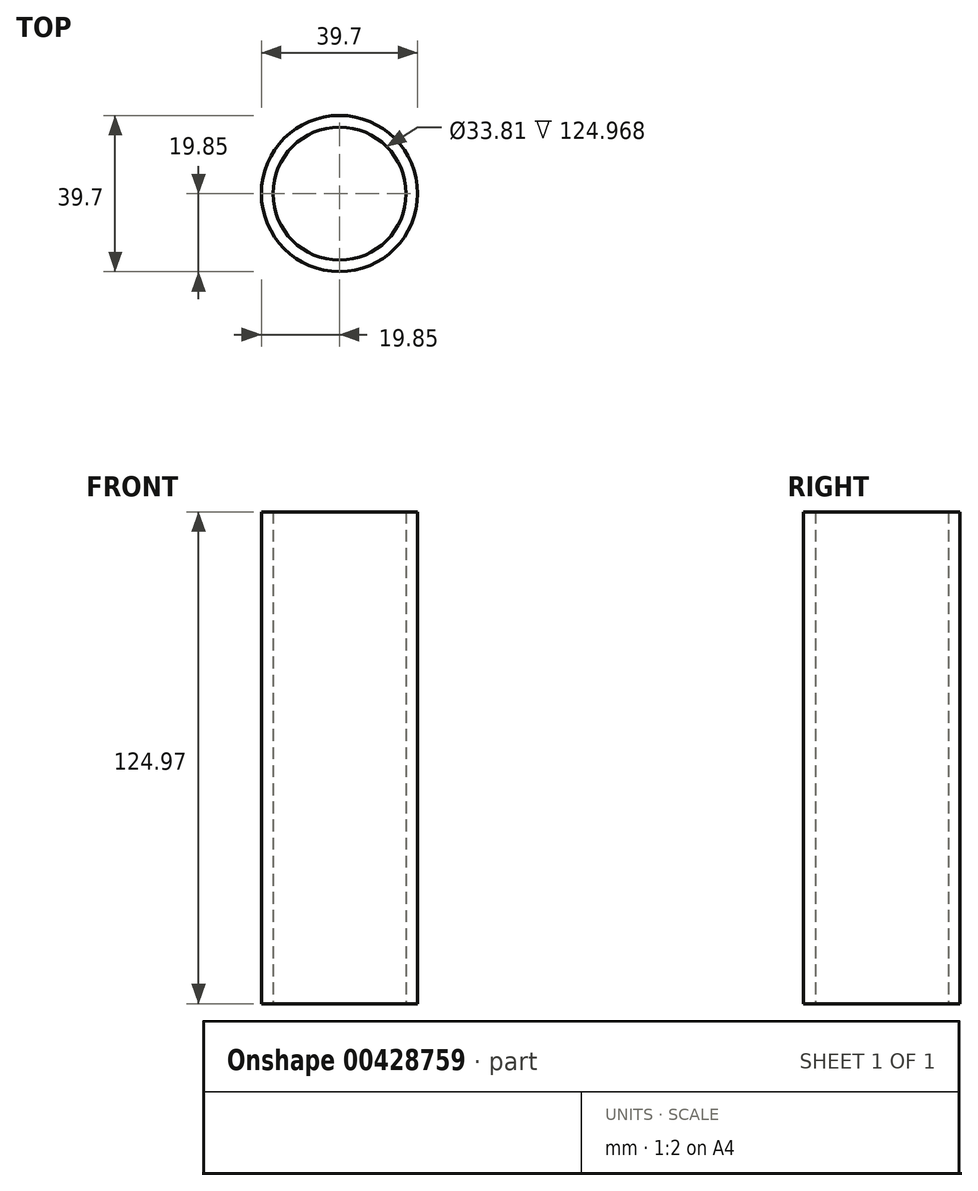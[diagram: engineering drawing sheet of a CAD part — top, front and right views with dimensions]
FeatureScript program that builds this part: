
annotation { "Feature Type Name" : "Feature", "Feature Type Description" : "" }
export const myFeature = defineFeature(function(context is Context, id is Id, definition is map)
    precondition{}
    {
        {
            var Q0;
            Q0=qCreatedBy(makeId("Top.planeOp"),FACE);
            var sketch = newSketch(context, id + "F0", { "sketchPlane" : qUnion([Q0])});
            skCircle(sketch, "E0", {"center": v(0, 0) * mm, "radius": 19.85 * mm});
            skCircle(sketch, "E1.0", {"center": v(0, 0) * mm, "radius": 16.9 * mm});
            skSolve(sketch);
        }
        {
            var Q0;
            Q0 = qSketchRegion(id + "F0", true);
            extrude(context, id + "F1", {"entities" : qUnion([Q0]), "depth" : 124.97 * mm});
        }
    });
